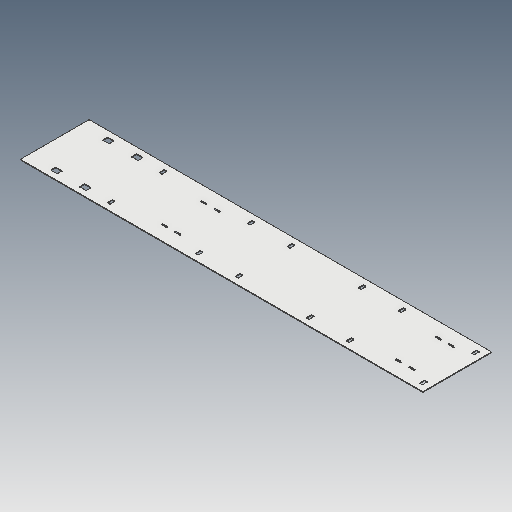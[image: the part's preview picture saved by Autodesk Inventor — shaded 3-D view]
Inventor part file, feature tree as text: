
AUTODESK INVENTOR PART (.ipt)
format: ipt  version: 2023.5 (Build 275446000, 446)  size: 202,240 bytes
history: native  units: in
note: dims shown in document units (in); Inventor stores cm internally (conversion verified against a paired STEP export)
features: mirror x1
ambient origin geometry x8: Origin, YZ Plane, XZ Plane, XY Plane, X Axis, Y Axis, Z Axis, Center Point
bodies: Solid1 (feature_tree)
feature tree (1):
  mirror  "Mirror1"
